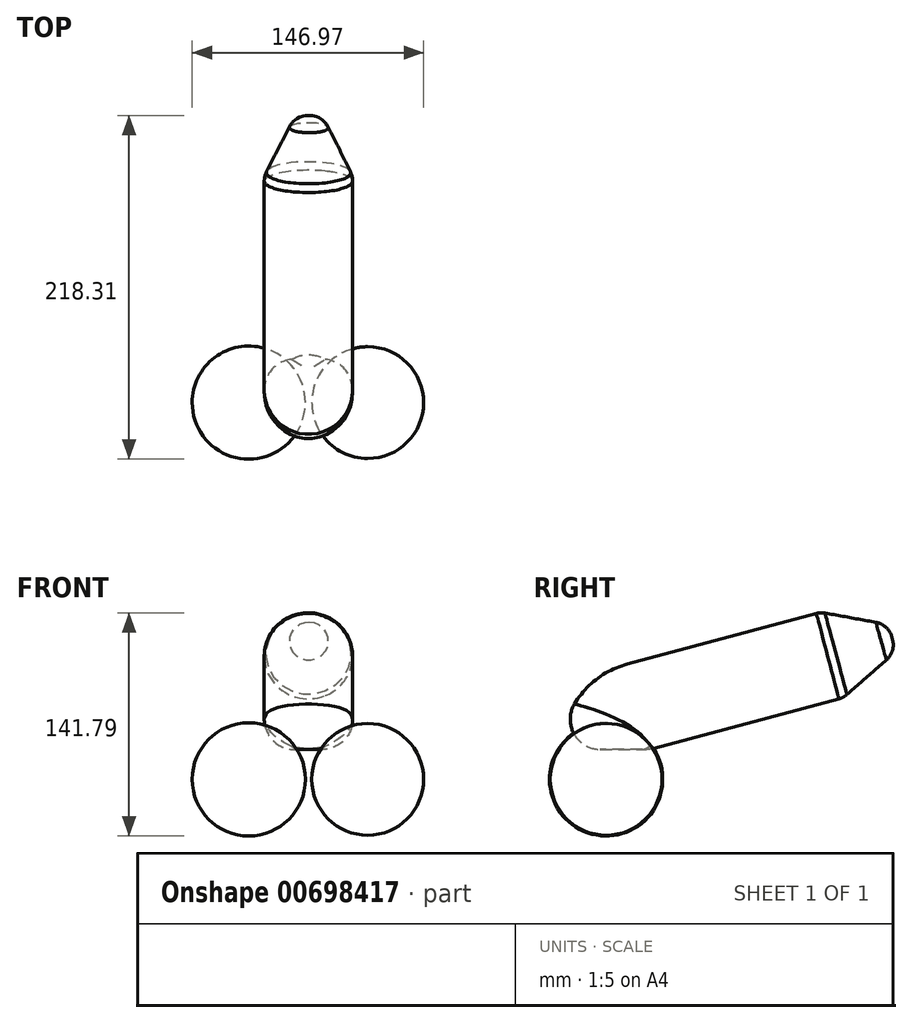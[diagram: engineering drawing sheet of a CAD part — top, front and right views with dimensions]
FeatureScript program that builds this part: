
annotation { "Feature Type Name" : "Feature", "Feature Type Description" : "" }
export const myFeature = defineFeature(function(context is Context, id is Id, definition is map)
    precondition{}
    {
        {
            var Q0;
            Q0=qCreatedBy(makeId("Top.planeOp"),FACE);
            var sketch = newSketch(context, id + "F0", { "sketchPlane" : qUnion([Q0])});
            skArc(sketch, "E0", {"start": v(0, -35.5) * mm, "mid": v(35.5, 0) * mm, "end": v(0, 35.5) * mm});
            skLineSegment(sketch, "E1", {"start": v(0, -35.5) * mm, "end": v(0, 35.5) * mm});
            skSolve(sketch);
        }
        {
            var Q0;
            Q0=makeQuery(id+"F0.imprint","IMPRINT",FACE,{"disambiguationData":[TD([[makeQuery(id+"F0.imprint","IMPRINT",EDGE,{"derivedFrom":sQuery(id+"F0.wireOp",EDGE,"E0")}),1.0]])]});
            var Q1;
            Q1=sQuery(id+"F0.wireOp",EDGE,"E1");
            revolve(context, id + "F1", {"entities" : qUnion([Q0]), "axis" : qUnion([Q1]), "revolveType" : RevolveType.FULL});
        }
        {
            var Q0;
            Q0=qCreatedBy(makeId("Top.planeOp"),FACE);
            var sketch = newSketch(context, id + "F2", { "sketchPlane" : qUnion([Q0])});
            skArc(sketch, "E2", {"start": v(-39.56, 0) * mm, "mid": v(-75.51, 35.95) * mm, "end": v(-111.46, 0) * mm});
            skLineSegment(sketch, "E3", {"start": v(-39.56, 0) * mm, "end": v(-111.46, 0) * mm});
            skSolve(sketch);
        }
        {
            var Q0;
            Q0=makeQuery(id+"F2.imprint","IMPRINT",FACE,{"disambiguationData":[TD([[makeQuery(id+"F2.imprint","IMPRINT",EDGE,{"derivedFrom":sQuery(id+"F2.wireOp",EDGE,"E2")}),1.0]])]});
            var Q1;
            Q1=sQuery(id+"F2.wireOp",EDGE,"E3");
            revolve(context, id + "F3", {"entities" : qUnion([Q0]), "axis" : qUnion([Q1]), "revolveType" : RevolveType.FULL});
        }
        {
            var Q0;
            Q0=qCreatedBy(makeId("Top.planeOp"),FACE);
            cPlane(context, id + "F4", {"entities" : qUnion([Q0]), "cplaneType" : CPlaneType.OFFSET, "offset" : 19.05 * mm, "width" : 152.4 * mm, "height" : 152.4 * mm});
        }
        {
            var Q0;
            Q0=qCreatedBy(id+"F4.planeOp",FACE);
            var sketch = newSketch(context, id + "F5", { "sketchPlane" : qUnion([Q0])});
            skCircle(sketch, "E4", {"center": v(-37.62, 0) * mm, "radius": 28.07 * mm});
            skLineSegment(sketch, "E5", {"start": v(-37.62, 0) * mm, "end": v(-37.62, 128.68) * mm, "construction": true});
            skLineSegment(sketch, "E6", {"start": v(-37.62, 28.07) * mm, "end": v(-122.1, 28.07) * mm});
            skSolve(sketch);
        }
        {
            var Q0;
            Q0=makeQuery(id+"F5.imprint","IMPRINT",FACE,{"disambiguationData":[TD([[makeQuery(id+"F5.imprint","IMPRINT",EDGE,{"derivedFrom":sQuery(id+"F5.wireOp",EDGE,"E4")}),1.0]])]});
            var Q1;
            Q1=sQuery(id+"F5.wireOp",EDGE,"E6");
            revolve(context, id + "F6", {"entities" : qUnion([Q0]), "axis" : qUnion([Q1]), "revolveType" : RevolveType.ONE_DIRECTION, "angle" : 75 * degree});
        }
        {
            var Q0;
            Q0=makeQuery(id+"F6.opRevolve","CAP_FACE",FACE,{"disambiguationData":[OSD([sQuery(id+"F5.wireOp",EDGE,"E4")])],"isStart":false});
            extrude(context, id + "F7", {"entities" : qUnion([Q0]), "operationType" : NewBodyOperationType.ADD, "depth" : 127 * mm, "offsetDistance" : 25.4 * mm});
        }
        {
            var Q0;
            Q0=makeQuery(id+"F7.opExtrude","CAP_FACE",FACE,{"disambiguationData":[OSD([sQuery(id+"F5.wireOp",EDGE,"E4")])],"isStart":false});
            var sketch = newSketch(context, id + "F8", { "sketchPlane" : qUnion([Q0])});
            skPoint(sketch, "E7", {"position": v(37.62, 39.2) * mm});
            skSolve(sketch);
        }
        {
            var Q0;
            Q0=makeQuery(id+"F8.imprint","IMPRINT",FACE,{"disambiguationData":[TD([[makeQuery(id+"F8.imprint","IMPRINT",EDGE,{"derivedFrom":makeQuery(id+"F7.opExtrude","CAP_EDGE",EDGE,{"disambiguationData":[OSD([sQuery(id+"F5.wireOp",EDGE,"E4")])],"isStart":false})}),1.0]])]});
            var sketch = newSketch(context, id + "F9", { "sketchPlane" : qUnion([Q0])});
            skCircle(sketch, "E8", {"center": v(37.33, 39.58) * mm, "radius": 8.96 * mm});
            skSolve(sketch);
        }
        {
            var Q0;
            Q0 = qSketchRegion(id + "F9", true);
            extrude(context, id + "F10", {"entities" : qUnion([Q0]), "operationType" : NewBodyOperationType.ADD, "depth" : 39.62 * mm, "offsetDistance" : 25.4 * mm});
        }
        {
            var Q1;
            Q1=makeQuery(id+"F10.opExtrude","CAP_FACE",FACE,{"disambiguationData":[OSD([sQuery(id+"F9.wireOp",EDGE,"E8")])],"isStart":false});
            var Q2;
            Q2=makeQuery(id+"F8.imprint","IMPRINT",FACE,{"disambiguationData":[TD([[makeQuery(id+"F8.imprint","IMPRINT",EDGE,{"derivedFrom":makeQuery(id+"F7.opExtrude","CAP_EDGE",EDGE,{"disambiguationData":[OSD([sQuery(id+"F5.wireOp",EDGE,"E4")])],"isStart":false})}),1.0]])]});
            loft(context, id + "F11", {"operationType" : NewBodyOperationType.ADD, "sheetProfilesArray" : [{ "sheetProfileEntities" : qUnion([Q1]) }, { "sheetProfileEntities" : qUnion([Q2]) }]});
        }
        {
            var Q0;
            {var subQ0=sQuery(id+"F5.wireOp",EDGE,"E4");Q0=makeQuery(id+"F11.boolean.opBoolean","MERGE",EDGE,{"derivedFrom":[makeQuery(id+"F7.opExtrude","CAP_EDGE",EDGE,{"disambiguationData":[OSD([subQ0])],"isStart":false}),makeQuery(id+"F11.opLoft","MID_CAP_EDGE",EDGE,{"disambiguationData":[OSD([subQ0,sQuery(id+"F9.wireOp",EDGE,"E8")])],"capPos":1.0})]});}
            var Q1;
            {var subQ0=sQuery(id+"F9.wireOp",EDGE,"E8");Q1=makeQuery(id+"F11.boolean.opBoolean","MERGE",EDGE,{"derivedFrom":[makeQuery(id+"F10.opExtrude","CAP_EDGE",EDGE,{"disambiguationData":[OSD([subQ0])],"isStart":false}),makeQuery(id+"F11.opLoft","MID_CAP_EDGE",EDGE,{"disambiguationData":[OSD([subQ0])],"capPos":0.0})]});}
            fillet(context, id + "F12", {"entities" : qUnion([Q0, Q1]), "radius" : 12.7 * mm, "tangentPropagation" : true, "allowEdgeOverflow" : false});
        }
        {
            var Q0;
            Q0=makeQuery(id+"F6.opRevolve","CAP_EDGE",EDGE,{"disambiguationData":[OSD([sQuery(id+"F5.wireOp",EDGE,"E4")])],"isStart":true});
            fillet(context, id + "F13", {"entities" : qUnion([Q0]), "radius" : 19.05 * mm, "tangentPropagation" : true, "allowEdgeOverflow" : false});
        }
    });
